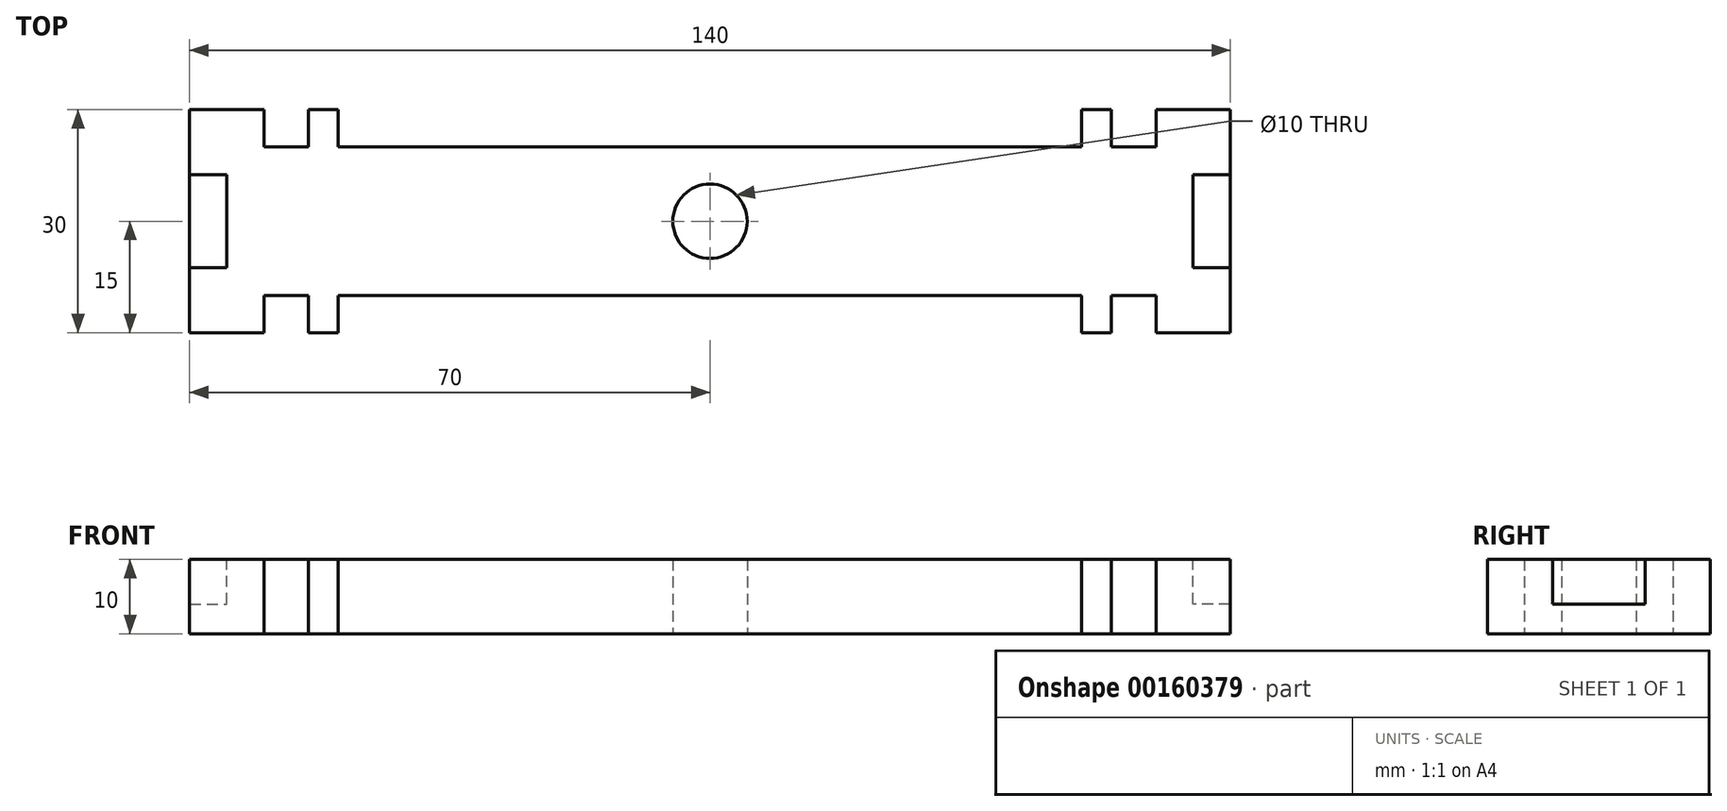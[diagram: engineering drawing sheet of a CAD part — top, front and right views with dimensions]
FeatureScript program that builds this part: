
annotation { "Feature Type Name" : "Feature", "Feature Type Description" : "" }
export const myFeature = defineFeature(function(context is Context, id is Id, definition is map)
    precondition{}
    {
        {
            var Q0;
            Q0=qCreatedBy(makeId("Top.planeOp"),FACE);
            var sketch = newSketch(context, id + "F0", { "sketchPlane" : qUnion([Q0])});
            skLineSegment(sketch, "E0", {"start": v(0, 0) * mm, "end": v(0, 21.43) * mm, "construction": true});
            skLineSegment(sketch, "E1.bottom", {"start": v(50, -10) * mm, "end": v(-50, -10) * mm});
            skLineSegment(sketch, "E1.top", {"start": v(50, 10) * mm, "end": v(-50, 10) * mm});
            skPoint(sketch, "E1.middle", {"position": v(0, 0) * mm});
            skLineSegment(sketch, "E2", {"start": v(0, 0) * mm, "end": v(111.88, 0) * mm, "construction": true});
            skLineSegment(sketch, "E3", {"start": v(50, 10) * mm, "end": v(50, 15) * mm});
            skLineSegment(sketch, "E4", {"start": v(50, 15) * mm, "end": v(54, 15) * mm});
            skLineSegment(sketch, "E5", {"start": v(54, 15) * mm, "end": v(54, 10) * mm});
            skLineSegment(sketch, "E6", {"start": v(54, 10) * mm, "end": v(60, 10) * mm});
            skLineSegment(sketch, "E7", {"start": v(60, 10) * mm, "end": v(60, 15) * mm});
            skLineSegment(sketch, "E8", {"start": v(70, 15) * mm, "end": v(70, 0) * mm});
            skLineSegment(sketch, "E9", {"start": v(60, 15) * mm, "end": v(70, 15) * mm});
            skLineSegment(sketch, "E10.MirrorCS", {"start": v(50, -10) * mm, "end": v(50, -15) * mm});
            skLineSegment(sketch, "E11.MirrorCS", {"start": v(54, -15) * mm, "end": v(54, -10) * mm});
            skLineSegment(sketch, "E12.MirrorCS", {"start": v(50, -15) * mm, "end": v(54, -15) * mm});
            skLineSegment(sketch, "E13.MirrorCS", {"start": v(60, -10) * mm, "end": v(60, -15) * mm});
            skLineSegment(sketch, "E14.MirrorCS", {"start": v(54, -10) * mm, "end": v(60, -10) * mm});
            skLineSegment(sketch, "E15.MirrorCS", {"start": v(60, -15) * mm, "end": v(70, -15) * mm});
            skLineSegment(sketch, "E16.MirrorCS", {"start": v(70, -15) * mm, "end": v(70, 0) * mm});
            skLineSegment(sketch, "E17.MirrorCS", {"start": v(-50, -15) * mm, "end": v(-54, -15) * mm});
            skLineSegment(sketch, "E18.MirrorCS", {"start": v(-60, -10) * mm, "end": v(-60, -15) * mm});
            skLineSegment(sketch, "E19.MirrorCS", {"start": v(-54, 15) * mm, "end": v(-54, 10) * mm});
            skLineSegment(sketch, "E20.MirrorCS", {"start": v(-50, 15) * mm, "end": v(-54, 15) * mm});
            skLineSegment(sketch, "E21.MirrorCS", {"start": v(-50, 10) * mm, "end": v(-50, 15) * mm});
            skLineSegment(sketch, "E22.MirrorCS", {"start": v(-60, 10) * mm, "end": v(-60, 15) * mm});
            skLineSegment(sketch, "E23.MirrorCS", {"start": v(-50, -10) * mm, "end": v(-50, -15) * mm});
            skLineSegment(sketch, "E24.MirrorCS", {"start": v(-54, -15) * mm, "end": v(-54, -10) * mm});
            skLineSegment(sketch, "E25.MirrorCS", {"start": v(-54, -10) * mm, "end": v(-60, -10) * mm});
            skLineSegment(sketch, "E26.MirrorCS", {"start": v(-54, 10) * mm, "end": v(-60, 10) * mm});
            skLineSegment(sketch, "E27.MirrorCS", {"start": v(-70, 15) * mm, "end": v(-70, 0) * mm});
            skLineSegment(sketch, "E28.MirrorCS", {"start": v(-60, 15) * mm, "end": v(-70, 15) * mm});
            skLineSegment(sketch, "E29.MirrorCS", {"start": v(-60, -15) * mm, "end": v(-70, -15) * mm});
            skLineSegment(sketch, "E30.MirrorCS", {"start": v(-70, -15) * mm, "end": v(-70, 0) * mm});
            skCircle(sketch, "E31", {"center": v(0, 0) * mm, "radius": 5 * mm});
            skSolve(sketch);
        }
        {
            var Q0;
            Q0 = qSketchRegion(id + "F0", true);
            extrude(context, id + "F1", {"entities" : qUnion([Q0]), "depth" : 10 * mm});
        }
        {
            var Q0;
            Q0=makeQuery(id+"F1.opExtrude","CAP_FACE",FACE,{"disambiguationData":[OSD([sQuery(id+"F0.wireOp",EDGE,"E1.bottom"),sQuery(id+"F0.wireOp",EDGE,"E1.top"),sQuery(id+"F0.wireOp",EDGE,"E3"),sQuery(id+"F0.wireOp",EDGE,"E4"),sQuery(id+"F0.wireOp",EDGE,"E5"),sQuery(id+"F0.wireOp",EDGE,"E6"),sQuery(id+"F0.wireOp",EDGE,"E7"),sQuery(id+"F0.wireOp",EDGE,"E8"),sQuery(id+"F0.wireOp",EDGE,"E9"),sQuery(id+"F0.wireOp",EDGE,"E10.MirrorCS"),sQuery(id+"F0.wireOp",EDGE,"E11.MirrorCS"),sQuery(id+"F0.wireOp",EDGE,"E12.MirrorCS"),sQuery(id+"F0.wireOp",EDGE,"E13.MirrorCS"),sQuery(id+"F0.wireOp",EDGE,"E14.MirrorCS"),sQuery(id+"F0.wireOp",EDGE,"E15.MirrorCS"),sQuery(id+"F0.wireOp",EDGE,"E16.MirrorCS"),sQuery(id+"F0.wireOp",EDGE,"E17.MirrorCS"),sQuery(id+"F0.wireOp",EDGE,"E18.MirrorCS"),sQuery(id+"F0.wireOp",EDGE,"E19.MirrorCS"),sQuery(id+"F0.wireOp",EDGE,"E20.MirrorCS"),sQuery(id+"F0.wireOp",EDGE,"E21.MirrorCS"),sQuery(id+"F0.wireOp",EDGE,"E22.MirrorCS"),sQuery(id+"F0.wireOp",EDGE,"E23.MirrorCS"),sQuery(id+"F0.wireOp",EDGE,"E24.MirrorCS"),sQuery(id+"F0.wireOp",EDGE,"E25.MirrorCS"),sQuery(id+"F0.wireOp",EDGE,"E26.MirrorCS"),sQuery(id+"F0.wireOp",EDGE,"E27.MirrorCS"),sQuery(id+"F0.wireOp",EDGE,"E28.MirrorCS"),sQuery(id+"F0.wireOp",EDGE,"E29.MirrorCS"),sQuery(id+"F0.wireOp",EDGE,"E30.MirrorCS"),sQuery(id+"F0.wireOp",EDGE,"E31")])],"isStart":false});
            var sketch = newSketch(context, id + "F2", { "sketchPlane" : qUnion([Q0])});
            skLineSegment(sketch, "E32", {"start": v(0, 0) * mm, "end": v(0, 49.16) * mm, "construction": true});
            skLineSegment(sketch, "E33.bottom", {"start": v(75, 6.25) * mm, "end": v(65, 6.25) * mm});
            skLineSegment(sketch, "E33.top", {"start": v(75, -6.25) * mm, "end": v(65, -6.25) * mm});
            skLineSegment(sketch, "E33.left", {"start": v(75, 6.25) * mm, "end": v(75, -6.25) * mm});
            skLineSegment(sketch, "E33.right", {"start": v(65, 6.25) * mm, "end": v(65, -6.25) * mm});
            skPoint(sketch, "E33.middle", {"position": v(70, 0) * mm});
            skPoint(sketch, "E34.MirrorP", {"position": v(-70, 0) * mm});
            skLineSegment(sketch, "E35.MirrorCS", {"start": v(-75, 6.25) * mm, "end": v(-65, 6.25) * mm});
            skLineSegment(sketch, "E36.MirrorCS", {"start": v(-75, -6.25) * mm, "end": v(-65, -6.25) * mm});
            skLineSegment(sketch, "E37.MirrorCS", {"start": v(-65, 6.25) * mm, "end": v(-65, -6.25) * mm});
            skLineSegment(sketch, "E38.MirrorCS", {"start": v(-75, 6.25) * mm, "end": v(-75, -6.25) * mm});
            skSolve(sketch);
        }
        {
            var Q0;
            Q0 = qSketchRegion(id + "F2", true);
            extrude(context, id + "F3", {"entities" : qUnion([Q0]), "operationType" : NewBodyOperationType.REMOVE, "oppositeDirection" : true, "depth" : 6 * mm});
        }
    });
